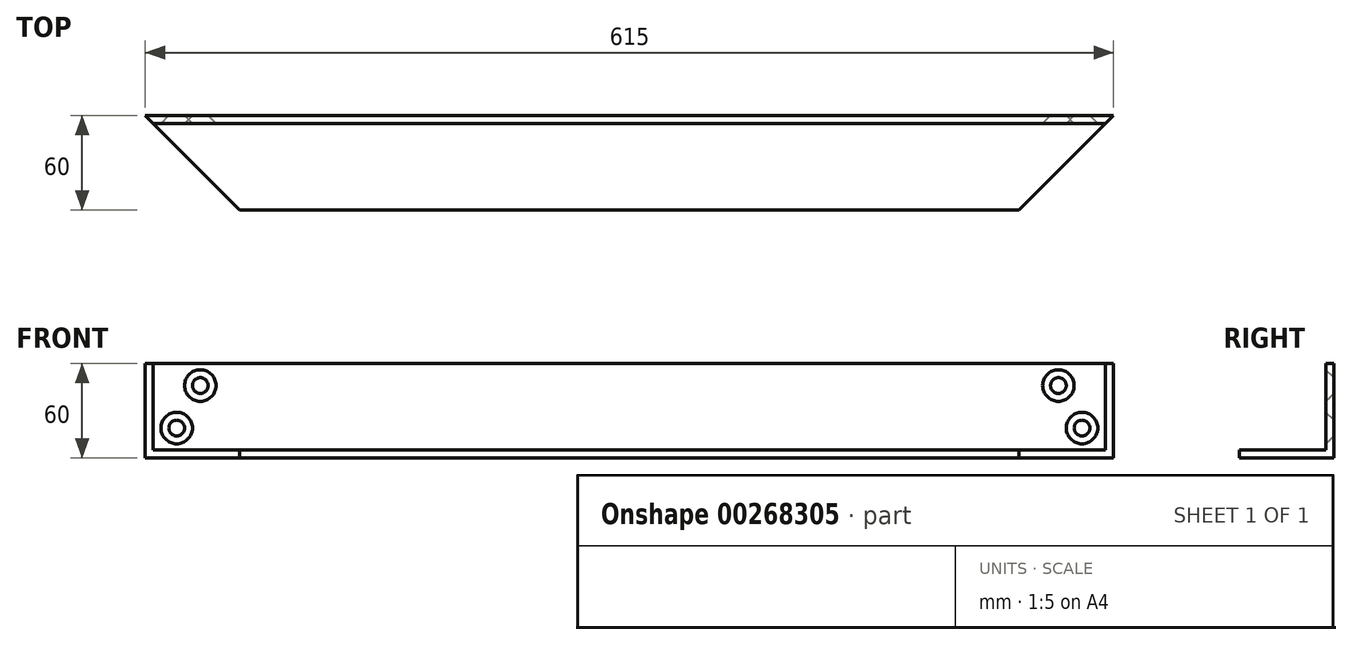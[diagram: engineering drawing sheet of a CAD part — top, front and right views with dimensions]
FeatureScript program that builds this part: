
annotation { "Feature Type Name" : "Feature", "Feature Type Description" : "" }
export const myFeature = defineFeature(function(context is Context, id is Id, definition is map)
    precondition{}
    {
        {
            var Q0;
            Q0=qCreatedBy(makeId("Right.planeOp"),FACE);
            var sketch = newSketch(context, id + "F0", { "sketchPlane" : qUnion([Q0])});
            skLineSegment(sketch, "E0", {"start": v(0, 0) * mm, "end": v(60, 0) * mm});
            skLineSegment(sketch, "E1", {"start": v(60, 0) * mm, "end": v(60, 60) * mm});
            skLineSegment(sketch, "E2", {"start": v(60, 60) * mm, "end": v(55, 60) * mm});
            skLineSegment(sketch, "E3", {"start": v(55, 60) * mm, "end": v(55, 5) * mm});
            skLineSegment(sketch, "E4", {"start": v(55, 5) * mm, "end": v(0, 5) * mm});
            skLineSegment(sketch, "E5", {"start": v(0, 5) * mm, "end": v(0, 0) * mm});
            skSolve(sketch);
        }
        {
            var Q0;
            Q0=makeQuery(id+"F0.imprint","IMPRINT",FACE,{"disambiguationData":[TD([[makeQuery(id+"F0.imprint","IMPRINT",EDGE,{"derivedFrom":sQuery(id+"F0.wireOp",EDGE,"E0")}),1.0]])]});
            extrude(context, id + "F1", {"entities" : qUnion([Q0]), "offsetDistance" : 25 * mm, "depth" : 615 * mm});
        }
        {
            var Q0;
            Q0=makeQuery(id+"F1.opExtrude","SWEPT_FACE",FACE,{"disambiguationData":[OSD([sQuery(id+"F0.wireOp",EDGE,"E0")])]});
            var sketch = newSketch(context, id + "F2", { "sketchPlane" : qUnion([Q0])});
            skLineSegment(sketch, "E6", {"start": v(0, -60) * mm, "end": v(60, 0) * mm});
            skLineSegment(sketch, "E7", {"start": v(60, 0) * mm, "end": v(0, 0) * mm});
            skLineSegment(sketch, "E8", {"start": v(0, 0) * mm, "end": v(0, -60) * mm});
            skLineSegment(sketch, "E9", {"start": v(615, -60) * mm, "end": v(615, 0) * mm});
            skLineSegment(sketch, "E10", {"start": v(615, 0) * mm, "end": v(555, 0) * mm});
            skLineSegment(sketch, "E11", {"start": v(555, 0) * mm, "end": v(615, -60) * mm});
            skSolve(sketch);
        }
        {
            var Q0;
            Q0 = qSketchRegion(id + "F2", true);
            var Q1;
            Q1=makeQuery(id+"F1.opExtrude","SWEPT_FACE",FACE,{"disambiguationData":[OSD([sQuery(id+"F0.wireOp",EDGE,"E2")])]});
            extrude(context, id + "F3", {"entities" : qUnion([Q0]), "operationType" : NewBodyOperationType.REMOVE, "endBound" : BoundingType.UP_TO_SURFACE, "oppositeDirection" : true, "endBoundEntityFace" : qUnion([Q1]), "depth" : 25 * mm});
        }
        {
            var Q0;
            Q0=makeQuery(id+"F1.opExtrude","SWEPT_FACE",FACE,{"disambiguationData":[OSD([sQuery(id+"F0.wireOp",EDGE,"E3")])]});
            var sketch = newSketch(context, id + "F4", { "sketchPlane" : qUnion([Q0])});
            skCircle(sketch, "E12", {"center": v(35, 46) * mm, "radius": 4.5 * mm});
            skCircle(sketch, "E13", {"center": v(20, 19) * mm, "radius": 4.5 * mm});
            skCircle(sketch, "E14", {"center": v(580, 46) * mm, "radius": 4.72 * mm});
            skCircle(sketch, "E15", {"center": v(595, 19) * mm, "radius": 5.29 * mm});
            skSolve(sketch);
        }
        {
            var Q0;
            Q0=sQuery(id+"F4.wireOp",VERTEX,"E12.center");
            var Q1;
            Q1=sQuery(id+"F4.wireOp",VERTEX,"E13.center");
            var Q2;
            Q2=sQuery(id+"F4.wireOp",VERTEX,"E14.center");
            var Q3;
            Q3=sQuery(id+"F4.wireOp",VERTEX,"E15.center");
            var Q4;
            Q4=makeQuery(id+"F1.opExtrude","SWEPT_BODY",BODY,{"disambiguationData":[OSD([sQuery(id+"F0.wireOp",EDGE,"E0"),sQuery(id+"F0.wireOp",EDGE,"E1"),sQuery(id+"F0.wireOp",EDGE,"E2"),sQuery(id+"F0.wireOp",EDGE,"E3"),sQuery(id+"F0.wireOp",EDGE,"E4"),sQuery(id+"F0.wireOp",EDGE,"E5")])]});
            hole(context, id + "F5", {"style" : HoleStyle.C_SINK, "endStyle" : HoleEndStyle.THROUGH, "holeDiameter" : 9 * mm, "cSinkDiameter" : 20 * mm, "cSinkAngle" : 90 * degree, "tappedDepth" : 12 * mm, "tapClearance" : 3, "locations" : qUnion([Q0, Q1, Q2, Q3]), "scope" : qUnion([Q4])});
        }
    });
